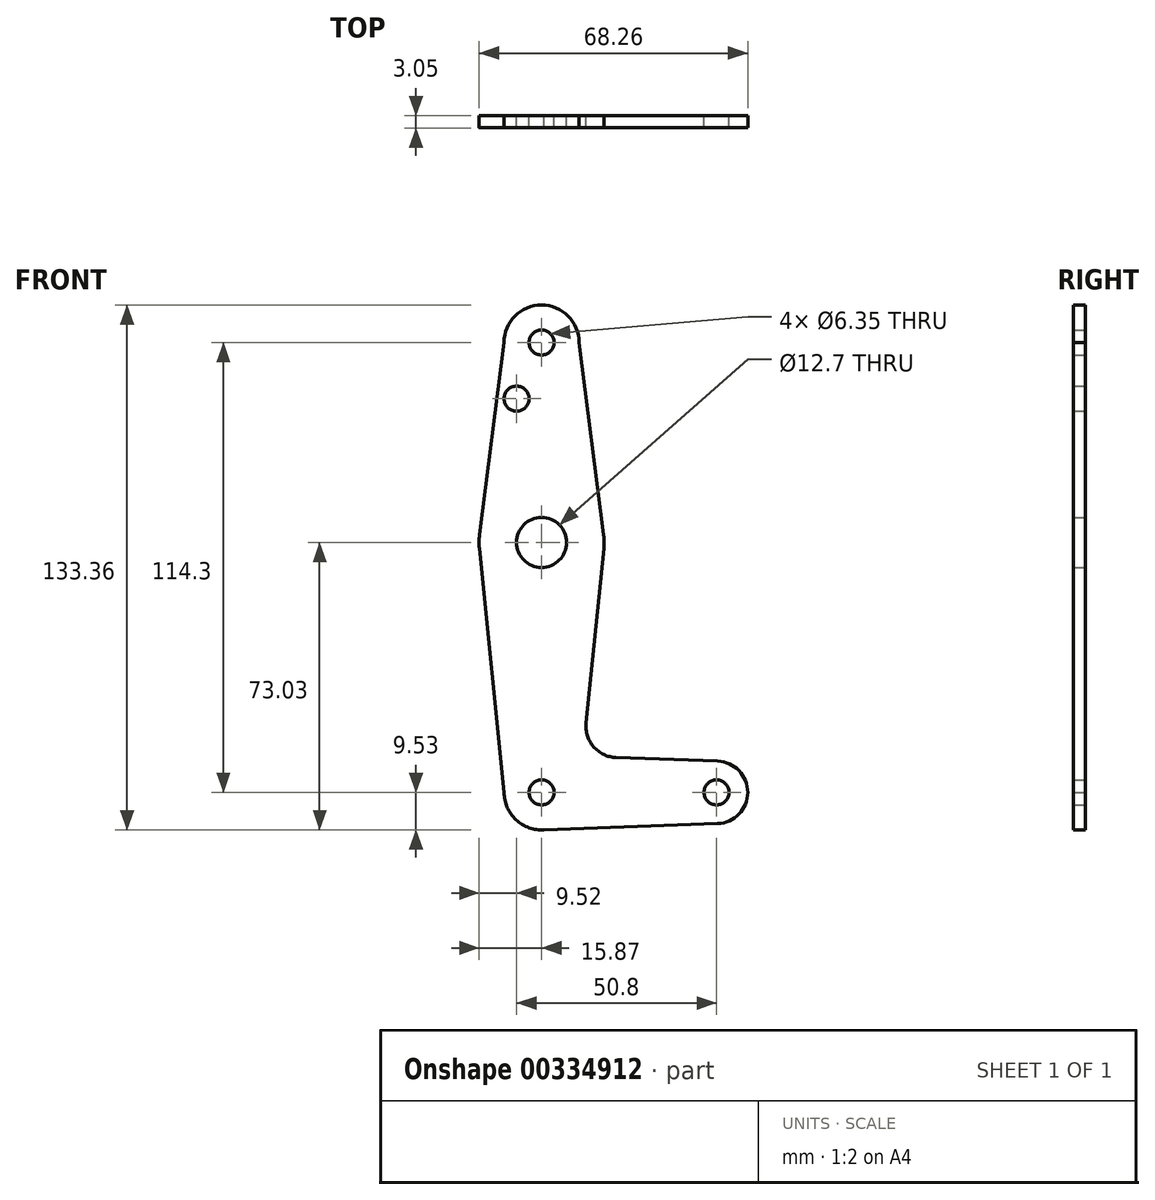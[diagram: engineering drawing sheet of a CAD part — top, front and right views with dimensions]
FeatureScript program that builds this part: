
annotation { "Feature Type Name" : "Feature", "Feature Type Description" : "" }
export const myFeature = defineFeature(function(context is Context, id is Id, definition is map)
    precondition{}
    {
        {
            var Q0;
            Q0=qCreatedBy(makeId("Front.planeOp"),FACE);
            var sketch = newSketch(context, id + "F0", { "sketchPlane" : qUnion([Q0])});
            skLineSegment(sketch, "E0", {"start": v(0, 0) * mm, "end": v(0, 114.3) * mm, "construction": true});
            skLineSegment(sketch, "E1", {"start": v(0, 0) * mm, "end": v(44.45, 0) * mm, "construction": true});
            skCircle(sketch, "E2", {"center": v(0, 114.3) * mm, "radius": 9.53 * mm});
            skCircle(sketch, "E3", {"center": v(0, 63.5) * mm, "radius": 15.88 * mm});
            skCircle(sketch, "E4", {"center": v(0, 0) * mm, "radius": 9.53 * mm});
            skCircle(sketch, "E5", {"center": v(44.45, 0) * mm, "radius": 7.94 * mm});
            skCircle(sketch, "E6", {"center": v(0, 114.3) * mm, "radius": 3.18 * mm});
            skCircle(sketch, "E7", {"center": v(0, 63.5) * mm, "radius": 6.35 * mm});
            skCircle(sketch, "E8", {"center": v(0, 0) * mm, "radius": 3.18 * mm});
            skCircle(sketch, "E9", {"center": v(44.45, 0) * mm, "radius": 3.18 * mm});
            skLineSegment(sketch, "E10", {"start": v(18.93, 8.85) * mm, "end": v(44.73, 7.93) * mm});
            skLineSegment(sketch, "E11", {"start": v(0, -9.52) * mm, "end": v(44.73, -7.93) * mm});
            skLineSegment(sketch, "E12", {"start": v(-9.53, 114.3) * mm, "end": v(-15.75, 65.5) * mm});
            skLineSegment(sketch, "E13", {"start": v(11.3, 17.6) * mm, "end": v(15.8, 61.9) * mm});
            skLineSegment(sketch, "E14", {"start": v(-9.53, 0) * mm, "end": v(-15.8, 61.9) * mm});
            skLineSegment(sketch, "E15", {"start": v(9.53, 114.3) * mm, "end": v(15.8, 65.14) * mm});
            skPoint(sketch, "E16.newPointB", {"position": v(0, 9.52) * mm});
            skArc(sketch, "E16.filletArc", {"start": v(11.3, 17.6) * mm, "mid": v(13.22, 11.57) * mm, "end": v(18.93, 8.85) * mm});
            skCircle(sketch, "E17", {"center": v(-6.35, 100.03) * mm, "radius": 3.18 * mm});
            skSolve(sketch);
        }
        {
            var Q0;
            Q0 = qSketchRegion(id + "F0", true);
            extrude(context, id + "F1", {"entities" : qUnion([Q0]), "depth" : 3.05 * mm});
        }
    });
